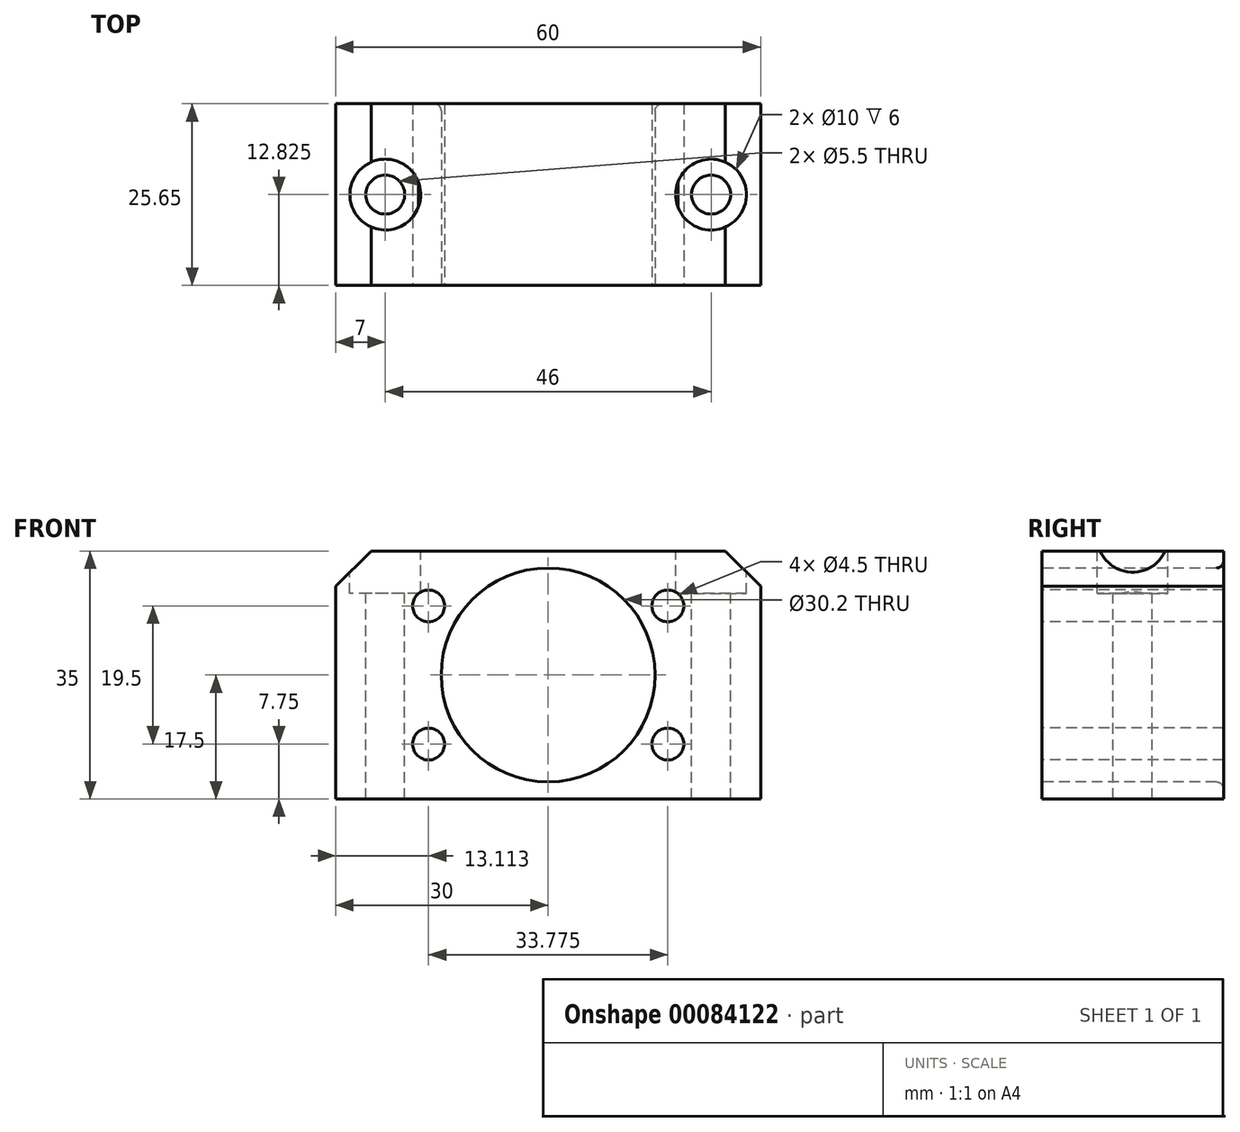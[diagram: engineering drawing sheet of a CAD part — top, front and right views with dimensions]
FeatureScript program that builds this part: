
annotation { "Feature Type Name" : "Feature", "Feature Type Description" : "" }
export const myFeature = defineFeature(function(context is Context, id is Id, definition is map)
    precondition{}
    {
        {
            var Q0;
            Q0=qCreatedBy(makeId("Front.planeOp"),FACE);
            var sketch = newSketch(context, id + "F0", { "sketchPlane" : qUnion([Q0])});
            skLineSegment(sketch, "E0.bottom", {"start": v(-30, -17.5) * mm, "end": v(30, -17.5) * mm});
            skLineSegment(sketch, "E0.top", {"start": v(-30, 17.5) * mm, "end": v(30, 17.5) * mm});
            skLineSegment(sketch, "E0.left", {"start": v(-30, -17.5) * mm, "end": v(-30, 17.5) * mm});
            skLineSegment(sketch, "E0.right", {"start": v(30, -17.5) * mm, "end": v(30, 17.5) * mm});
            skPoint(sketch, "E0.middle", {"position": v(0, 0) * mm});
            skLineSegment(sketch, "E1", {"start": v(-30, 0) * mm, "end": v(30, 0) * mm, "construction": true});
            skCircle(sketch, "E2", {"center": v(0, 0) * mm, "radius": 15.1 * mm});
            skCircle(sketch, "E3", {"center": v(0, 0) * mm, "radius": 19.5 * mm, "construction": true});
            skLineSegment(sketch, "E4", {"start": v(0, 0) * mm, "end": v(16.89, 9.75) * mm, "construction": true});
            skCircle(sketch, "E5", {"center": v(16.89, 9.75) * mm, "radius": 2.25 * mm});
            skCircle(sketch, "E6.MirrorC", {"center": v(-16.89, 9.75) * mm, "radius": 2.25 * mm});
            skCircle(sketch, "E7.MirrorC", {"center": v(16.89, -9.75) * mm, "radius": 2.25 * mm});
            skCircle(sketch, "E8.MirrorC", {"center": v(-16.89, -9.75) * mm, "radius": 2.25 * mm});
            skSolve(sketch);
        }
        {
            var Q0;
            Q0=makeQuery(id+"F0.imprint","IMPRINT",FACE,{"disambiguationData":[TD([[makeQuery(id+"F0.imprint","IMPRINT",EDGE,{"derivedFrom":sQuery(id+"F0.wireOp",EDGE,"E0.bottom")}),1.0]])]});
            extrude(context, id + "F1", {"entities" : qUnion([Q0]), "oppositeDirection" : true, "depth" : 25.65 * mm});
        }
        {
            var Q0;
            Q0=makeQuery(id+"F1.opExtrude","SWEPT_FACE",FACE,{"disambiguationData":[OSD([sQuery(id+"F0.wireOp",EDGE,"E0.top")])]});
            var sketch = newSketch(context, id + "F2", { "sketchPlane" : qUnion([Q0])});
            skLineSegment(sketch, "E9", {"start": v(-30, 12.82) * mm, "end": v(30, 12.82) * mm, "construction": true});
            skLineSegment(sketch, "E10", {"start": v(0, 25.65) * mm, "end": v(0, 0) * mm, "construction": true});
            skPoint(sketch, "E11", {"position": v(-23, 12.82) * mm});
            skPoint(sketch, "E12.MirrorP", {"position": v(23, 12.82) * mm});
            skSolve(sketch);
        }
        {
            var Q0;
            Q0=sQuery(id+"F2.wireOp",VERTEX,"E11");
            var Q1;
            Q1=sQuery(id+"F2.wireOp",VERTEX,"E12.MirrorP");
            var Q2;
            Q2=makeQuery(id+"F1.opExtrude","SWEPT_BODY",BODY,{"disambiguationData":[OSD([sQuery(id+"F0.wireOp",EDGE,"E0.bottom"),sQuery(id+"F0.wireOp",EDGE,"E0.top"),sQuery(id+"F0.wireOp",EDGE,"E0.left"),sQuery(id+"F0.wireOp",EDGE,"E0.right"),sQuery(id+"F0.wireOp",EDGE,"E2"),sQuery(id+"F0.wireOp",EDGE,"E5"),sQuery(id+"F0.wireOp",EDGE,"E6.MirrorC"),sQuery(id+"F0.wireOp",EDGE,"E7.MirrorC"),sQuery(id+"F0.wireOp",EDGE,"E8.MirrorC")])]});
            hole(context, id + "F3", {"style" : HoleStyle.C_BORE, "endStyle" : HoleEndStyle.BLIND, "holeDiameter" : 5.5 * mm, "cBoreDiameter" : 10 * mm, "cBoreDepth" : 6 * mm, "holeDepth" : 35 * mm, "isTappedThrough" : true, "tappedDepth" : 12 * mm, "tapClearance" : 3, "startFromSketch" : true, "locations" : qUnion([Q0, Q1]), "scope" : qUnion([Q2])});
        }
        {
            var Q0;
            Q0=makeQuery(id+"F1.opExtrude","SWEPT_EDGE",EDGE,{"disambiguationData":[OSD([sQuery(id+"F0.wireOp",EDGE,"E0.top"),sQuery(id+"F0.wireOp",EDGE,"E0.right")])]});
            var Q1;
            Q1=makeQuery(id+"F1.opExtrude","SWEPT_EDGE",EDGE,{"disambiguationData":[OSD([sQuery(id+"F0.wireOp",EDGE,"E0.top"),sQuery(id+"F0.wireOp",EDGE,"E0.left")])]});
            chamfer(context, id + "F4", {"entities" : qUnion([Q0, Q1]), "width" : 5 * mm, "tangentPropagation" : true});
        }
        {
            var Q0;
            Q0=makeQuery(id+"F1.opExtrude","CAP_EDGE",EDGE,{"disambiguationData":[OSD([sQuery(id+"F0.wireOp",EDGE,"E2")])],"isStart":false});
            fillet(context, id + "F5", {"entities" : qUnion([Q0]), "radius" : 1 * mm, "tangentPropagation" : true, "allowEdgeOverflow" : false});
        }
    });
